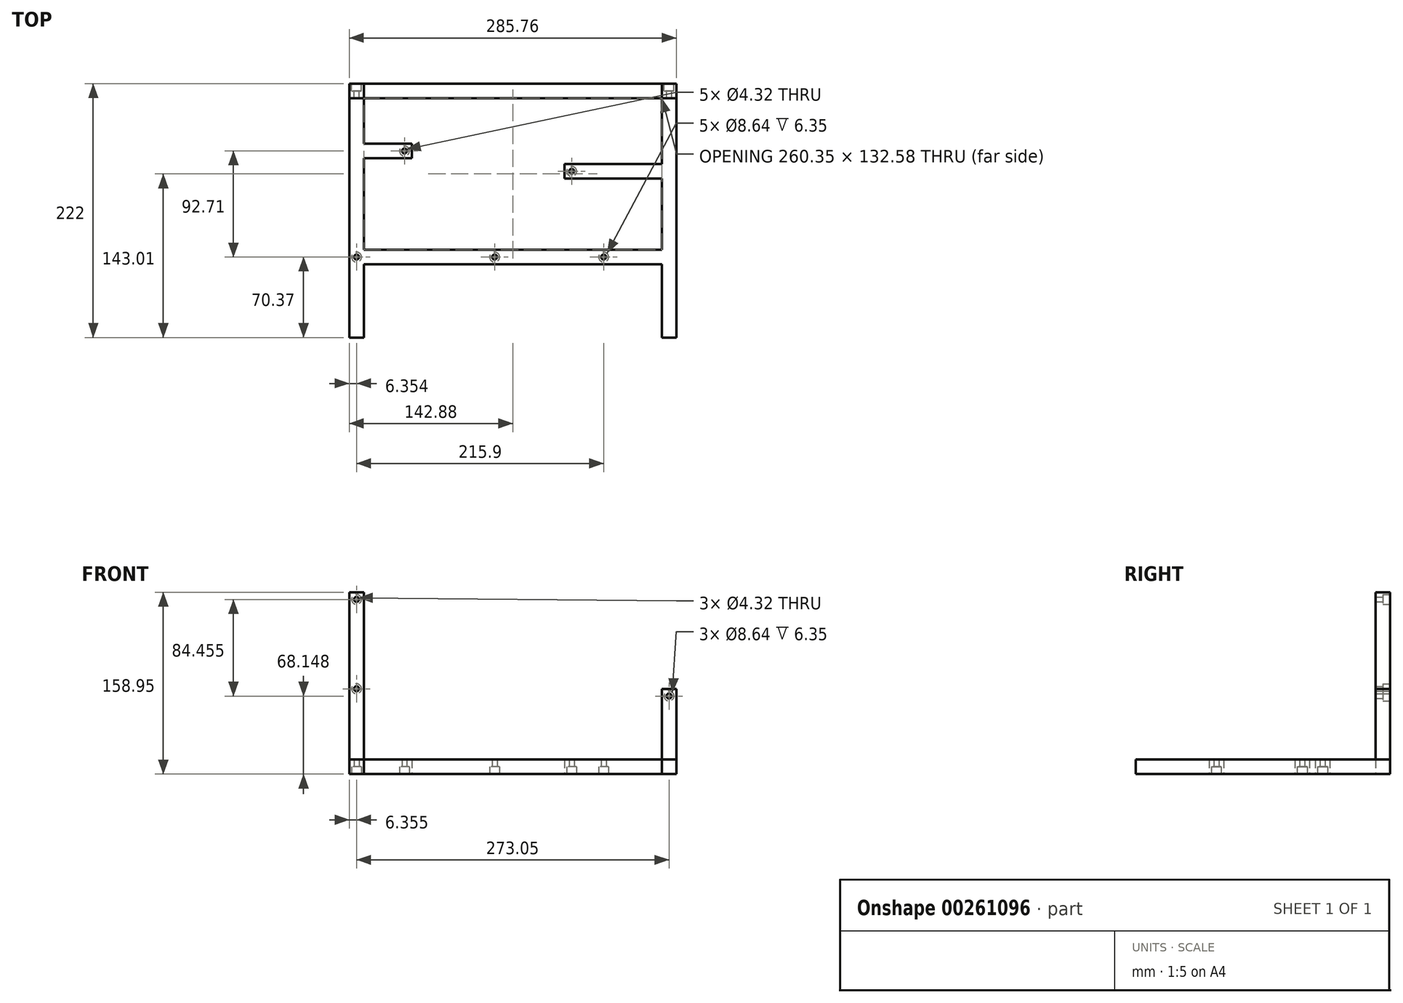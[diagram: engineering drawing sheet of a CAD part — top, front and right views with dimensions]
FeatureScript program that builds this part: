
annotation { "Feature Type Name" : "Feature", "Feature Type Description" : "" }
export const myFeature = defineFeature(function(context is Context, id is Id, definition is map)
    precondition{}
    {
        {
            var Q0;
            Q0=qCreatedBy(makeId("Top.planeOp"),FACE);
            var sketch = newSketch(context, id + "F0", { "sketchPlane" : qUnion([Q0])});
            skLineSegment(sketch, "E0.top", {"start": v(-142.88, -215.65) * mm, "end": v(-130.17, -215.65) * mm});
            skLineSegment(sketch, "E1.top", {"start": v(130.17, -215.65) * mm, "end": v(142.88, -215.65) * mm});
            skLineSegment(sketch, "E2.bottom", {"start": v(-130.17, 6.35) * mm, "end": v(130.17, 6.35) * mm});
            skLineSegment(sketch, "E2.top", {"start": v(-130.17, -6.35) * mm, "end": v(130.17, -6.35) * mm});
            skLineSegment(sketch, "E2.left", {"start": v(-130.18, 6.35) * mm, "end": v(-130.18, -6.35) * mm});
            skLineSegment(sketch, "E2.right", {"start": v(130.17, 6.35) * mm, "end": v(130.17, -6.35) * mm});
            skPoint(sketch, "E3", {"position": v(-130.17, 0) * mm});
            skPoint(sketch, "E4", {"position": v(0, 6.35) * mm});
            skPoint(sketch, "E5", {"position": v(130.17, 0) * mm});
            skLineSegment(sketch, "E6", {"start": v(-130.17, 6.35) * mm, "end": v(-142.88, 6.35) * mm});
            skLineSegment(sketch, "E7", {"start": v(-130.17, -6.35) * mm, "end": v(-142.88, -6.35) * mm});
            skLineSegment(sketch, "E8", {"start": v(130.17, 6.35) * mm, "end": v(142.87, 6.35) * mm});
            skLineSegment(sketch, "E9", {"start": v(130.17, -6.35) * mm, "end": v(142.87, -6.35) * mm});
            skLineSegment(sketch, "E10", {"start": v(-130.18, -215.65) * mm, "end": v(-130.18, -6.35) * mm});
            skLineSegment(sketch, "E11", {"start": v(-142.88, 6.35) * mm, "end": v(-142.88, -215.65) * mm});
            skLineSegment(sketch, "E12", {"start": v(142.87, 6.35) * mm, "end": v(142.87, -6.35) * mm});
            skLineSegment(sketch, "E13", {"start": v(142.88, -215.65) * mm, "end": v(142.87, -6.35) * mm});
            skLineSegment(sketch, "E14", {"start": v(130.17, -6.35) * mm, "end": v(130.17, -215.65) * mm});
            skLineSegment(sketch, "E15", {"start": v(-142.88, 6.35) * mm, "end": v(-142.88, -6.35) * mm});
            skLineSegment(sketch, "E16.bottom", {"start": v(-142.88, -215.65) * mm, "end": v(142.88, -215.65) * mm});
            skLineSegment(sketch, "E16.top", {"start": v(-142.88, -228.35) * mm, "end": v(142.88, -228.35) * mm});
            skLineSegment(sketch, "E16.left", {"start": v(-142.88, -215.65) * mm, "end": v(-142.88, -228.35) * mm});
            skLineSegment(sketch, "E16.right", {"start": v(142.87, -215.65) * mm, "end": v(142.87, -228.35) * mm});
            skLineSegment(sketch, "E17", {"start": v(130.17, -215.65) * mm, "end": v(130.17, -228.35) * mm});
            skLineSegment(sketch, "E18", {"start": v(-130.18, -215.65) * mm, "end": v(-130.18, -228.35) * mm});
            skLineSegment(sketch, "E19.bottom", {"start": v(130.17, -64) * mm, "end": v(45.08, -64) * mm});
            skLineSegment(sketch, "E19.top", {"start": v(130.17, -76.7) * mm, "end": v(45.08, -76.7) * mm});
            skLineSegment(sketch, "E19.left", {"start": v(130.17, -64) * mm, "end": v(130.17, -76.7) * mm});
            skLineSegment(sketch, "E19.right", {"start": v(45.08, -64) * mm, "end": v(45.08, -76.7) * mm});
            skLineSegment(sketch, "E20.bottom", {"start": v(-130.18, -46.22) * mm, "end": v(-88.27, -46.22) * mm});
            skLineSegment(sketch, "E20.top", {"start": v(-130.18, -58.92) * mm, "end": v(-88.27, -58.92) * mm});
            skLineSegment(sketch, "E20.left", {"start": v(-130.18, -46.22) * mm, "end": v(-130.18, -58.92) * mm});
            skLineSegment(sketch, "E20.right", {"start": v(-88.27, -46.22) * mm, "end": v(-88.27, -58.92) * mm});
            skLineSegment(sketch, "E21.bottom", {"start": v(130.17, -138.93) * mm, "end": v(-130.18, -138.93) * mm});
            skLineSegment(sketch, "E21.top", {"start": v(130.17, -151.63) * mm, "end": v(-130.18, -151.63) * mm});
            skLineSegment(sketch, "E21.left", {"start": v(130.17, -138.93) * mm, "end": v(130.17, -151.63) * mm});
            skLineSegment(sketch, "E21.right", {"start": v(-130.18, -138.93) * mm, "end": v(-130.18, -151.63) * mm});
            skCircle(sketch, "E22", {"center": v(-94.62, -52.57) * mm, "radius": 4.32 * mm});
            skPoint(sketch, "E23", {"position": v(-88.27, -52.57) * mm});
            skCircle(sketch, "E24", {"center": v(-94.62, -52.57) * mm, "radius": 2.16 * mm});
            skPoint(sketch, "E25", {"position": v(-136.53, -52.57) * mm});
            skPoint(sketch, "E26", {"position": v(-136.53, -6.85) * mm});
            skPoint(sketch, "E27", {"position": v(-136.53, 6.35) * mm});
            skCircle(sketch, "E28", {"center": v(51.43, -70.35) * mm, "radius": 4.32 * mm});
            skCircle(sketch, "E29", {"center": v(51.43, -70.35) * mm, "radius": 2.16 * mm});
            skPoint(sketch, "E30", {"position": v(45.08, -70.35) * mm});
            skCircle(sketch, "E31", {"center": v(79.37, -145.28) * mm, "radius": 2.16 * mm});
            skCircle(sketch, "E32", {"center": v(-15.88, -145.28) * mm, "radius": 2.16 * mm});
            skCircle(sketch, "E33", {"center": v(-136.53, -145.28) * mm, "radius": 2.16 * mm});
            skCircle(sketch, "E34", {"center": v(-136.53, -145.28) * mm, "radius": 4.32 * mm});
            skCircle(sketch, "E35", {"center": v(-15.88, -145.28) * mm, "radius": 4.32 * mm});
            skCircle(sketch, "E36", {"center": v(79.37, -145.28) * mm, "radius": 4.32 * mm});
            skPoint(sketch, "E37", {"position": v(130.17, -145.28) * mm});
            skLineSegment(sketch, "E38", {"start": v(-130.18, -151.63) * mm, "end": v(-142.88, -151.63) * mm});
            skLineSegment(sketch, "E39", {"start": v(130.17, -151.63) * mm, "end": v(142.87, -151.63) * mm});
            skSolve(sketch);
        }
        {
            var Q0;
            {var subQ0=sQuery(id+"F0.wireOp",EDGE,"E0.bottom");Q0=makeQuery(id+"F0.imprint","IMPRINT",FACE,{"disambiguationData":[TD([[makeQuery(id+"F0.imprint","IMPRINT",EDGE,{"derivedFrom":subQ0}),-1.0]])]});}
            var Q1;
            {var subQ0=sQuery(id+"F0.wireOp",EDGE,"E0.top");Q1=makeQuery(id+"F0.imprint","IMPRINT",FACE,{"disambiguationData":[TD([[makeQuery(id+"F0.imprint","IMPRINT",EDGE,{"derivedFrom":subQ0}),1.0]])]});}
            var Q2;
            Q2=makeQuery(id+"F0.imprint","IMPRINT",FACE,{"disambiguationData":[TD([[makeQuery(id+"F0.imprint","IMPRINT",EDGE,{"derivedFrom":sQuery(id+"F0.wireOp",EDGE,"E2.bottom")}),-1.0]])]});
            var Q3;
            {var subQ0=sQuery(id+"F0.wireOp",EDGE,"E1.bottom");Q3=makeQuery(id+"F0.imprint","IMPRINT",FACE,{"disambiguationData":[TD([[makeQuery(id+"F0.imprint","IMPRINT",EDGE,{"derivedFrom":subQ0}),-1.0]])]});}
            var Q4;
            {var subQ0=sQuery(id+"F0.wireOp",EDGE,"E1.top");Q4=makeQuery(id+"F0.imprint","IMPRINT",FACE,{"disambiguationData":[TD([[makeQuery(id+"F0.imprint","IMPRINT",EDGE,{"derivedFrom":subQ0}),1.0]])]});}
            var Q5;
            Q5=makeQuery(id+"F0.imprint","IMPRINT",FACE,{"disambiguationData":[TD([[makeQuery(id+"F0.imprint","IMPRINT",EDGE,{"derivedFrom":sQuery(id+"F0.wireOp",EDGE,"E2.left")}),-1.0]])]});
            var Q6;
            Q6=makeQuery(id+"F0.imprint","IMPRINT",FACE,{"disambiguationData":[TD([[makeQuery(id+"F0.imprint","IMPRINT",EDGE,{"derivedFrom":sQuery(id+"F0.wireOp",EDGE,"E2.right")}),1.0]])]});
            var Q7;
            Q7=makeQuery(id+"F0.imprint","IMPRINT",FACE,{"disambiguationData":[TD([[makeQuery(id+"F0.imprint","IMPRINT",EDGE,{"derivedFrom":sQuery(id+"F0.wireOp",EDGE,"E7")}),1.0]])]});
            var Q8;
            Q8=makeQuery(id+"F0.imprint","IMPRINT",FACE,{"disambiguationData":[TD([[makeQuery(id+"F0.imprint","IMPRINT",EDGE,{"derivedFrom":sQuery(id+"F0.wireOp",EDGE,"E9")}),-1.0]])]});
            var Q9;
            Q9=makeQuery(id+"F0.imprint","IMPRINT",FACE,{"disambiguationData":[TD([[makeQuery(id+"F0.imprint","IMPRINT",EDGE,{"derivedFrom":sQuery(id+"F0.wireOp",EDGE,"E20.bottom")}),-1.0]])]});
            var Q10;
            Q10=makeQuery(id+"F0.imprint","IMPRINT",FACE,{"disambiguationData":[TD([[makeQuery(id+"F0.imprint","IMPRINT",EDGE,{"derivedFrom":sQuery(id+"F0.wireOp",EDGE,"E19.bottom")}),1.0]])]});
            var Q11;
            Q11=makeQuery(id+"F0.imprint","IMPRINT",FACE,{"disambiguationData":[TD([[makeQuery(id+"F0.imprint","IMPRINT",EDGE,{"derivedFrom":sQuery(id+"F0.wireOp",EDGE,"E21.bottom")}),1.0]])]});
            var Q12;
            Q12=makeQuery(id+"F0.imprint","IMPRINT",FACE,{"disambiguationData":[TD([[makeQuery(id+"F0.imprint","IMPRINT",EDGE,{"derivedFrom":sQuery(id+"F0.wireOp",EDGE,"E22")}),1.0]])]});
            var Q13;
            Q13=makeQuery(id+"F0.imprint","IMPRINT",FACE,{"disambiguationData":[TD([[makeQuery(id+"F0.imprint","IMPRINT",EDGE,{"derivedFrom":sQuery(id+"F0.wireOp",EDGE,"E32")}),-1.0]])]});
            var Q14;
            Q14=makeQuery(id+"F0.imprint","IMPRINT",FACE,{"disambiguationData":[TD([[makeQuery(id+"F0.imprint","IMPRINT",EDGE,{"derivedFrom":sQuery(id+"F0.wireOp",EDGE,"E31")}),-1.0]])]});
            var Q15;
            Q15=makeQuery(id+"F0.imprint","IMPRINT",FACE,{"disambiguationData":[TD([[makeQuery(id+"F0.imprint","IMPRINT",EDGE,{"derivedFrom":sQuery(id+"F0.wireOp",EDGE,"E28")}),1.0]])]});
            var Q16;
            Q16=makeQuery(id+"F0.imprint","IMPRINT",FACE,{"disambiguationData":[TD([[makeQuery(id+"F0.imprint","IMPRINT",EDGE,{"derivedFrom":sQuery(id+"F0.wireOp",EDGE,"E33")}),-1.0]])]});
            extrude(context, id + "F1", {"entities" : qUnion([Q0, Q1, Q2, Q3, Q4, Q5, Q6, Q7, Q8, Q9, Q10, Q11, Q12, Q13, Q14, Q15, Q16]), "depth" : 12.7 * mm, "offsetDistance" : 25.4 * mm});
        }
        {
            var Q0;
            Q0=makeQuery(id+"F1.opExtrude","CAP_FACE",FACE,{"disambiguationData":[OSD([sQuery(id+"F0.wireOp",EDGE,"E0.bottom"),sQuery(id+"F0.wireOp",EDGE,"E0.top"),sQuery(id+"F0.wireOp",EDGE,"E0.left"),sQuery(id+"F0.wireOp",EDGE,"E0.right"),sQuery(id+"F0.wireOp",EDGE,"E1.bottom"),sQuery(id+"F0.wireOp",EDGE,"E1.top"),sQuery(id+"F0.wireOp",EDGE,"E1.left"),sQuery(id+"F0.wireOp",EDGE,"E1.right"),sQuery(id+"F0.wireOp",EDGE,"E2.bottom"),sQuery(id+"F0.wireOp",EDGE,"E2.top")])],"isStart":false});
            var sketch = newSketch(context, id + "F2", { "sketchPlane" : qUnion([Q0])});
            skLineSegment(sketch, "E40.bottom", {"start": v(-142.87, 6.35) * mm, "end": v(-142.88, 6.35) * mm});
            skLineSegment(sketch, "E40.top", {"start": v(-130.17, -6.35) * mm, "end": v(-142.87, -6.35) * mm});
            skLineSegment(sketch, "E40.left", {"start": v(-130.17, 6.35) * mm, "end": v(-130.17, -6.35) * mm});
            skLineSegment(sketch, "E40.right", {"start": v(-142.87, 6.35) * mm, "end": v(-142.87, -6.35) * mm});
            skLineSegment(sketch, "E41.bottom", {"start": v(130.17, -6.35) * mm, "end": v(142.88, -6.35) * mm});
            skLineSegment(sketch, "E41.top", {"start": v(130.17, 6.35) * mm, "end": v(142.88, 6.35) * mm});
            skLineSegment(sketch, "E41.left", {"start": v(130.17, -6.35) * mm, "end": v(130.17, 6.35) * mm});
            skLineSegment(sketch, "E41.right", {"start": v(142.88, -6.35) * mm, "end": v(142.88, 6.35) * mm});
            skLineSegment(sketch, "E42.bottom", {"start": v(-142.88, -58.92) * mm, "end": v(-130.18, -58.92) * mm});
            skLineSegment(sketch, "E42.top", {"start": v(-142.88, -46.22) * mm, "end": v(-130.18, -46.22) * mm});
            skLineSegment(sketch, "E42.left", {"start": v(-142.88, -58.92) * mm, "end": v(-142.88, -46.22) * mm});
            skLineSegment(sketch, "E42.right", {"start": v(-130.18, -58.92) * mm, "end": v(-130.18, -46.22) * mm});
            skLineSegment(sketch, "E43.bottom", {"start": v(142.87, -76.7) * mm, "end": v(130.17, -76.7) * mm});
            skLineSegment(sketch, "E43.top", {"start": v(142.87, -64) * mm, "end": v(130.17, -64) * mm});
            skLineSegment(sketch, "E43.left", {"start": v(142.87, -76.7) * mm, "end": v(142.87, -64) * mm});
            skLineSegment(sketch, "E43.right", {"start": v(130.17, -76.7) * mm, "end": v(130.17, -64) * mm});
            skSolve(sketch);
        }
        {
            var Q0;
            Q0=makeQuery(id+"F2.imprint","IMPRINT",FACE,{"disambiguationData":[TD([[makeQuery(id+"F2.imprint","IMPRINT",EDGE,{"derivedFrom":sQuery(id+"F2.wireOp",EDGE,"E40.top")}),-1.0]])]});
            extrude(context, id + "F3", {"entities" : qUnion([Q0]), "depth" : 146.25 * mm, "offsetDistance" : 25.4 * mm});
        }
        {
            var Q0;
            {var subQ0=sQuery(id+"F2.wireOp",EDGE,"E41.left");Q0=makeQuery(id+"F2.imprint","IMPRINT",FACE,{"disambiguationData":[TD([[makeQuery(id+"F2.imprint","IMPRINT",EDGE,{"derivedFrom":subQ0}),-1.0]])]});}
            extrude(context, id + "F4", {"entities" : qUnion([Q0]), "depth" : 61.8 * mm, "offsetDistance" : 25.4 * mm});
        }
        {
            var Q0;
            Q0=makeQuery(id+"F3.opExtrude","SWEPT_FACE",FACE,{"disambiguationData":[OSD([sQuery(id+"F0.wireOp",EDGE,"E2.bottom"),sQuery(id+"F0.wireOp",EDGE,"E6")])]});
            var sketch = newSketch(context, id + "F5", { "sketchPlane" : qUnion([Q0])});
            skCircle(sketch, "E44", {"center": v(136.52, 152.6) * mm, "radius": 4.32 * mm});
            skCircle(sketch, "E45", {"center": v(136.52, 152.6) * mm, "radius": 2.16 * mm});
            skCircle(sketch, "E46", {"center": v(136.52, 74.5) * mm, "radius": 2.16 * mm});
            skCircle(sketch, "E47", {"center": v(136.52, 74.5) * mm, "radius": 4.32 * mm});
            skPoint(sketch, "E48", {"position": v(136.52, 158.95) * mm});
            skSolve(sketch);
        }
        {
            var Q0;
            Q0=makeQuery(id+"F4.opExtrude","SWEPT_FACE",FACE,{"disambiguationData":[OSD([sQuery(id+"F2.wireOp",EDGE,"E41.top")])]});
            var sketch = newSketch(context, id + "F6", { "sketchPlane" : qUnion([Q0])});
            skCircle(sketch, "E49", {"center": v(-136.53, 68.15) * mm, "radius": 2.16 * mm});
            skCircle(sketch, "E50", {"center": v(-136.53, 68.15) * mm, "radius": 4.32 * mm});
            skSolve(sketch);
        }
        {
            var Q0;
            Q0=makeQuery(id+"F6.imprint","IMPRINT",FACE,{"disambiguationData":[TD([[makeQuery(id+"F6.imprint","IMPRINT",EDGE,{"derivedFrom":sQuery(id+"F6.wireOp",EDGE,"E49")}),1.0]])]});
            extrude(context, id + "F7", {"entities" : qUnion([Q0]), "operationType" : NewBodyOperationType.REMOVE, "endBound" : BoundingType.UP_TO_NEXT, "oppositeDirection" : true, "depth" : 25.4 * mm, "offsetDistance" : 25.4 * mm});
        }
        {
            var Q0;
            Q0=makeQuery(id+"F5.imprint","IMPRINT",FACE,{"disambiguationData":[TD([[makeQuery(id+"F5.imprint","IMPRINT",EDGE,{"derivedFrom":sQuery(id+"F5.wireOp",EDGE,"E45")}),1.0]])]});
            var Q1;
            Q1=makeQuery(id+"F5.imprint","IMPRINT",FACE,{"disambiguationData":[TD([[makeQuery(id+"F5.imprint","IMPRINT",EDGE,{"derivedFrom":sQuery(id+"F5.wireOp",EDGE,"E46")}),1.0]])]});
            extrude(context, id + "F8", {"entities" : qUnion([Q0, Q1]), "operationType" : NewBodyOperationType.REMOVE, "endBound" : BoundingType.UP_TO_NEXT, "oppositeDirection" : true, "depth" : 25.4 * mm});
        }
        {
            var Q0;
            Q0=makeQuery(id+"F6.imprint","IMPRINT",FACE,{"disambiguationData":[TD([[makeQuery(id+"F6.imprint","IMPRINT",EDGE,{"derivedFrom":sQuery(id+"F6.wireOp",EDGE,"eoDmcJSq-L7UF-Ox9Z-J71m-2etQZwR1YTlI")}),-1.0]])]});
            var Q1;
            Q1=makeQuery(id+"F6.imprint","IMPRINT",FACE,{"disambiguationData":[TD([[makeQuery(id+"F6.imprint","IMPRINT",EDGE,{"derivedFrom":sQuery(id+"F6.wireOp",EDGE,"E49")}),-1.0]])]});
            extrude(context, id + "F9", {"entities" : qUnion([Q0, Q1]), "operationType" : NewBodyOperationType.REMOVE, "oppositeDirection" : true, "depth" : 6.35 * mm, "offsetDistance" : 25.4 * mm});
        }
        {
            var Q0;
            Q0=makeQuery(id+"F5.imprint","IMPRINT",FACE,{"disambiguationData":[TD([[makeQuery(id+"F5.imprint","IMPRINT",EDGE,{"derivedFrom":sQuery(id+"F5.wireOp",EDGE,"E44")}),1.0]])]});
            var Q1;
            Q1=makeQuery(id+"F5.imprint","IMPRINT",FACE,{"disambiguationData":[TD([[makeQuery(id+"F5.imprint","IMPRINT",EDGE,{"derivedFrom":sQuery(id+"F5.wireOp",EDGE,"E46")}),-1.0]])]});
            extrude(context, id + "F10", {"entities" : qUnion([Q0, Q1]), "operationType" : NewBodyOperationType.REMOVE, "oppositeDirection" : true, "depth" : 6.35 * mm});
        }
        {
            var Q0;
            Q0=makeQuery(id+"F0.imprint","IMPRINT",FACE,{"disambiguationData":[TD([[makeQuery(id+"F0.imprint","IMPRINT",EDGE,{"derivedFrom":sQuery(id+"F0.wireOp",EDGE,"E33")}),-1.0]])]});
            var Q1;
            Q1=makeQuery(id+"F0.imprint","IMPRINT",FACE,{"disambiguationData":[TD([[makeQuery(id+"F0.imprint","IMPRINT",EDGE,{"derivedFrom":sQuery(id+"F0.wireOp",EDGE,"E32")}),-1.0]])]});
            var Q2;
            Q2=makeQuery(id+"F0.imprint","IMPRINT",FACE,{"disambiguationData":[TD([[makeQuery(id+"F0.imprint","IMPRINT",EDGE,{"derivedFrom":sQuery(id+"F0.wireOp",EDGE,"E31")}),-1.0]])]});
            var Q3;
            Q3=makeQuery(id+"F0.imprint","IMPRINT",FACE,{"disambiguationData":[TD([[makeQuery(id+"F0.imprint","IMPRINT",EDGE,{"derivedFrom":sQuery(id+"F0.wireOp",EDGE,"E28")}),1.0]])]});
            var Q4;
            Q4=makeQuery(id+"F0.imprint","IMPRINT",FACE,{"disambiguationData":[TD([[makeQuery(id+"F0.imprint","IMPRINT",EDGE,{"derivedFrom":sQuery(id+"F0.wireOp",EDGE,"E22")}),1.0]])]});
            extrude(context, id + "F11", {"entities" : qUnion([Q0, Q1, Q2, Q3, Q4]), "operationType" : NewBodyOperationType.REMOVE, "depth" : 6.35 * mm});
        }
    });
